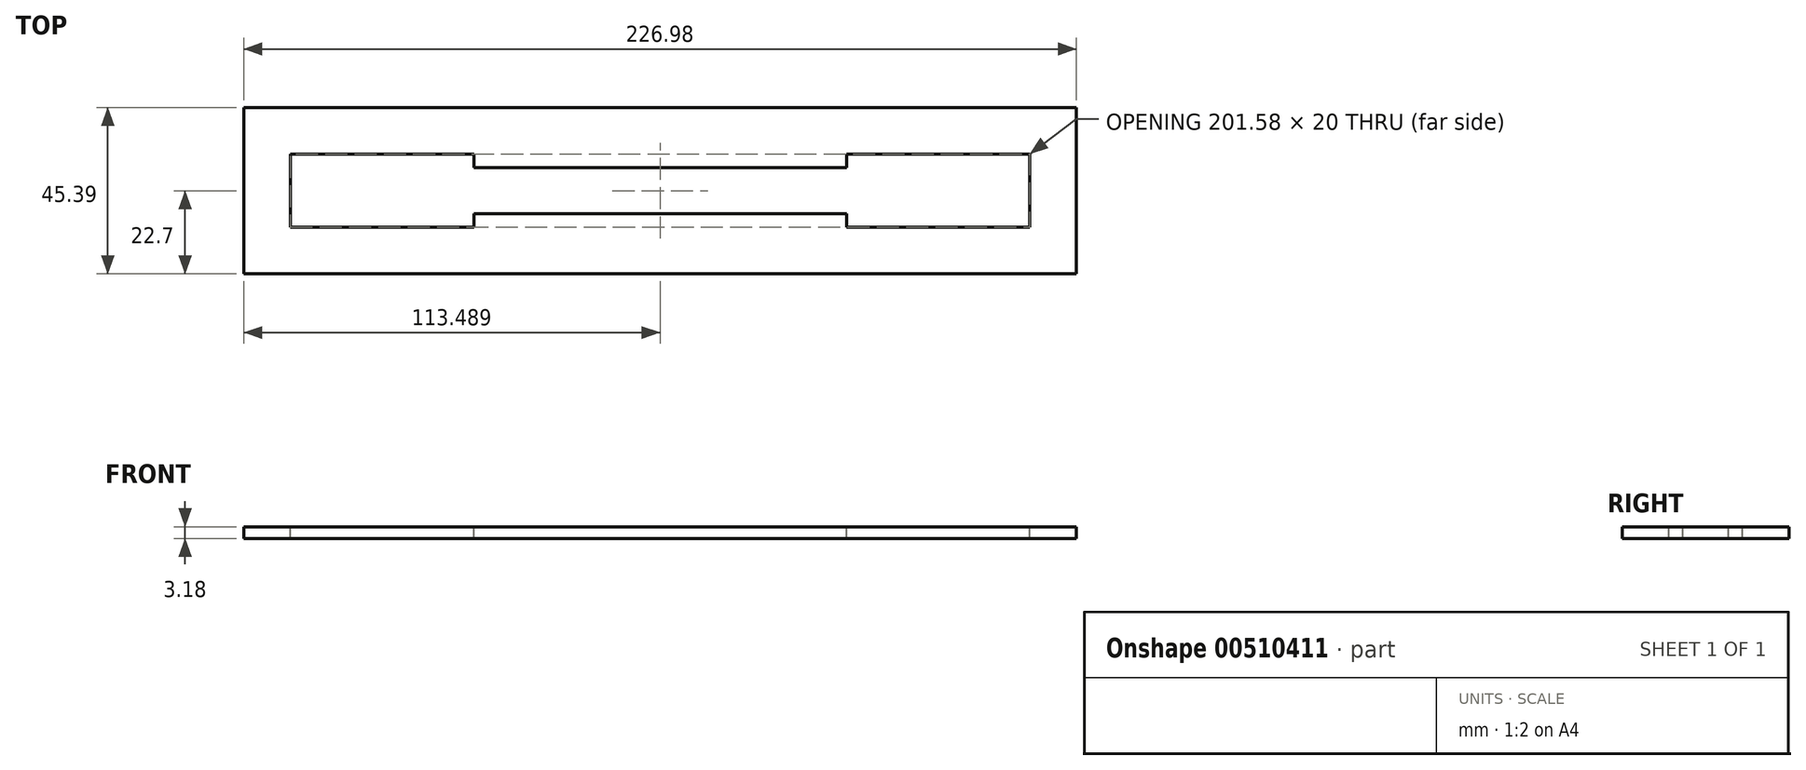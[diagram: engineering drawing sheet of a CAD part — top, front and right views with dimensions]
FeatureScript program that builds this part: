
annotation { "Feature Type Name" : "Feature", "Feature Type Description" : "" }
export const myFeature = defineFeature(function(context is Context, id is Id, definition is map)
    precondition{}
    {
        {
            var Q0;
            Q0=qCreatedBy(makeId("Top.planeOp"),FACE);
            var sketch = newSketch(context, id + "F0", { "sketchPlane" : qUnion([Q0])});
            skLineSegment(sketch, "E0.bottom", {"start": v(0, 0) * mm, "end": v(226.98, 0) * mm});
            skLineSegment(sketch, "E0.top", {"start": v(0, 45.39) * mm, "end": v(226.98, 45.39) * mm});
            skLineSegment(sketch, "E0.left", {"start": v(0, 0) * mm, "end": v(0, 45.39) * mm});
            skLineSegment(sketch, "E0.right", {"start": v(226.98, 0) * mm, "end": v(226.98, 45.39) * mm});
            skSolve(sketch);
        }
        {
            var Q0;
            Q0 = qSketchRegion(id + "F0", true);
            extrude(context, id + "F1", {"entities" : qUnion([Q0]), "depth" : 3.17 * mm});
        }
        {
            var Q0;
            Q0=makeQuery(id+"F1.opExtrude","CAP_FACE",FACE,{"disambiguationData":[OSD([sQuery(id+"F0.wireOp",EDGE,"E0.bottom"),sQuery(id+"F0.wireOp",EDGE,"E0.top"),sQuery(id+"F0.wireOp",EDGE,"E0.left"),sQuery(id+"F0.wireOp",EDGE,"E0.right")])],"isStart":false});
            var sketch = newSketch(context, id + "F2", { "sketchPlane" : qUnion([Q0])});
            skLineSegment(sketch, "E1", {"start": v(0, 0) * mm, "end": v(0, 12.7) * mm, "construction": true});
            skLineSegment(sketch, "E2", {"start": v(0, 12.7) * mm, "end": v(12.7, 12.7) * mm, "construction": true});
            skLineSegment(sketch, "E3", {"start": v(12.7, 12.7) * mm, "end": v(12.7, 32.7) * mm});
            skLineSegment(sketch, "E4", {"start": v(12.7, 32.7) * mm, "end": v(62.7, 32.7) * mm});
            skLineSegment(sketch, "E5", {"start": v(62.7, 32.7) * mm, "end": v(62.7, 28.95) * mm});
            skLineSegment(sketch, "E6", {"start": v(62.7, 28.95) * mm, "end": v(72.03, 28.95) * mm});
            skLineSegment(sketch, "E7", {"start": v(72.03, 28.95) * mm, "end": v(154.95, 28.95) * mm});
            skLineSegment(sketch, "E8", {"start": v(154.95, 28.95) * mm, "end": v(164.28, 28.95) * mm});
            skLineSegment(sketch, "E9", {"start": v(164.28, 28.95) * mm, "end": v(164.28, 32.7) * mm});
            skLineSegment(sketch, "E10", {"start": v(214.28, 32.7) * mm, "end": v(164.28, 32.7) * mm});
            skLineSegment(sketch, "E11", {"start": v(12.7, 32.7) * mm, "end": v(0, 32.7) * mm, "construction": true});
            skLineSegment(sketch, "E12", {"start": v(0, 32.7) * mm, "end": v(0, 45.39) * mm, "construction": true});
            skLineSegment(sketch, "E13", {"start": v(214.28, 32.7) * mm, "end": v(226.98, 32.7) * mm, "construction": true});
            skLineSegment(sketch, "E14", {"start": v(226.98, 32.7) * mm, "end": v(226.98, 45.39) * mm, "construction": true});
            skLineSegment(sketch, "E15", {"start": v(214.28, 32.7) * mm, "end": v(214.28, 12.7) * mm});
            skLineSegment(sketch, "E16", {"start": v(12.7, 12.7) * mm, "end": v(62.7, 12.7) * mm});
            skLineSegment(sketch, "E17", {"start": v(214.28, 12.7) * mm, "end": v(164.28, 12.7) * mm});
            skLineSegment(sketch, "E18", {"start": v(62.7, 12.7) * mm, "end": v(62.7, 16.45) * mm});
            skLineSegment(sketch, "E19", {"start": v(62.7, 16.45) * mm, "end": v(72.03, 16.45) * mm});
            skLineSegment(sketch, "E20", {"start": v(72.03, 16.45) * mm, "end": v(154.95, 16.45) * mm});
            skLineSegment(sketch, "E21", {"start": v(154.95, 16.45) * mm, "end": v(164.28, 16.45) * mm});
            skLineSegment(sketch, "E22", {"start": v(164.28, 16.45) * mm, "end": v(164.28, 12.7) * mm});
            skSolve(sketch);
        }
        {
            var Q0;
            Q0=makeQuery(id+"F2.imprint","IMPRINT",FACE,{"disambiguationData":[TD([[makeQuery(id+"F2.imprint","IMPRINT",EDGE,{"derivedFrom":sQuery(id+"F2.wireOp",EDGE,"E3")}),-1.0]])]});
            extrude(context, id + "F3", {"entities" : qUnion([Q0]), "operationType" : NewBodyOperationType.REMOVE, "oppositeDirection" : true, "depth" : 25.4 * mm});
        }
    });
